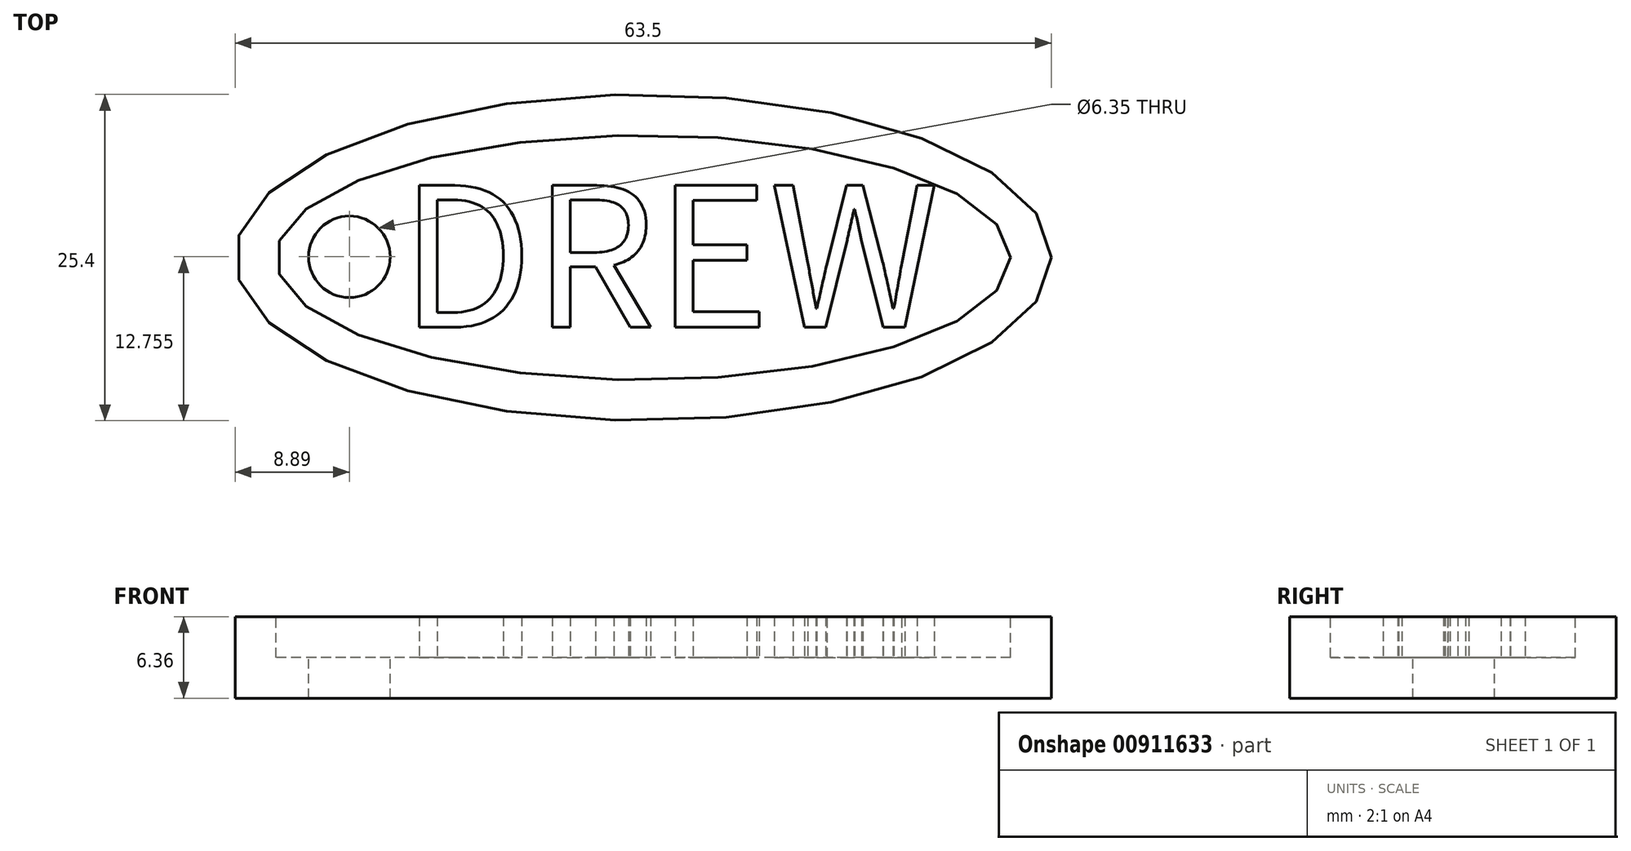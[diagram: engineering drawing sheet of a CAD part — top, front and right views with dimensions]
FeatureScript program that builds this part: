
annotation { "Feature Type Name" : "Feature", "Feature Type Description" : "" }
export const myFeature = defineFeature(function(context is Context, id is Id, definition is map)
    precondition{}
    {
        {
            var Q0;
            Q0=qCreatedBy(makeId("Top.planeOp"),FACE);
            var sketch = newSketch(context, id + "F0", { "sketchPlane" : qUnion([Q0])});
            skEllipse(sketch, "E0", {"center": v(0, 0) * mm, "majorRadius": 31.75 * mm, "minorRadius": 12.7 * mm, "majorAxis": v(1, 0)});
            skSolve(sketch);
        }
        {
            var Q0;
            Q0=makeQuery(id+"F0.imprint","IMPRINT",FACE,{"disambiguationData":[TD([[makeQuery(id+"F0.imprint","IMPRINT",EDGE,{"derivedFrom":sQuery(id+"F0.wireOp",EDGE,"E0")}),1.0]])]});
            extrude(context, id + "F1", {"entities" : qUnion([Q0]), "endBound" : BoundingType.SYMMETRIC, "depth" : 6.35 * mm, "offsetDistance" : 25.4 * mm});
        }
        {
            var Q0;
            Q0=makeQuery(id+"F1.opExtrude","CAP_FACE",FACE,{"disambiguationData":[OSD([sQuery(id+"F0.wireOp",EDGE,"E0")])],"isStart":false});
            var sketch = newSketch(context, id + "F2", { "sketchPlane" : qUnion([Q0])});
            skEllipse(sketch, "E1", {"center": v(0, 0) * mm, "majorRadius": 28.58 * mm, "minorRadius": 9.53 * mm, "majorAxis": v(1, 0)});
            skSolve(sketch);
        }
        {
            var Q0;
            Q0 = qSketchRegion(id + "F2", true);
            extrude(context, id + "F3", {"entities" : qUnion([Q0]), "operationType" : NewBodyOperationType.REMOVE, "oppositeDirection" : true, "depth" : 3.17 * mm, "offsetDistance" : 25.4 * mm});
        }
        {
            var Q0;
            Q0=makeQuery(id+"F3.boolean.opBoolean","COPY",FACE,{"derivedFrom":makeQuery(id+"F3.opExtrude","CAP_FACE",FACE,{"disambiguationData":[OSD([sQuery(id+"F2.wireOp",EDGE,"E1")])],"isStart":false})});
            var sketch = newSketch(context, id + "F4", { "sketchPlane" : qUnion([Q0])});
            skSolve(sketch);
        }
        {
            var Q0;
            Q0=makeQuery(id+"F4.imprint","IMPRINT",FACE,{"disambiguationData":[TD([[makeQuery(id+"F4.imprint","IMPRINT",EDGE,{"derivedFrom":makeQuery(id+"F3.boolean.opBoolean","COPY",EDGE,{"derivedFrom":makeQuery(id+"F3.opExtrude","CAP_EDGE",EDGE,{"disambiguationData":[OSD([sQuery(id+"F2.wireOp",EDGE,"E1")])],"isStart":false})})}),1.0]])]});
            var sketch = newSketch(context, id + "F5", { "sketchPlane" : qUnion([Q0])});
            skText(sketch, "E2", { "text": "DREW", "fontName": "NotoSansCJKsc-Regular.otf"});
            const initialGuessF5  = {"E2": [-0.01893, -0.00542, 1, 0, 0.01084]};
            skSetInitialGuess(sketch, initialGuessF5);
            skSolve(sketch);
        }
        {
            var Q0;
            Q0 = qSketchRegion(id + "F5", true);
            extrude(context, id + "F6", {"entities" : qUnion([Q0]), "operationType" : NewBodyOperationType.ADD, "depth" : 3.17 * mm, "offsetDistance" : 25.4 * mm});
        }
        {
            var Q0;
            Q0=makeQuery(id+"F4.imprint","IMPRINT",FACE,{"disambiguationData":[TD([[makeQuery(id+"F4.imprint","IMPRINT",EDGE,{"derivedFrom":makeQuery(id+"F3.boolean.opBoolean","COPY",EDGE,{"derivedFrom":makeQuery(id+"F3.opExtrude","CAP_EDGE",EDGE,{"disambiguationData":[OSD([sQuery(id+"F2.wireOp",EDGE,"E1")])],"isStart":false})})}),1.0]])]});
            var sketch = newSketch(context, id + "F7", { "sketchPlane" : qUnion([Q0])});
            skCircle(sketch, "E3", {"center": v(-22.86, 0.05) * mm, "radius": 3.18 * mm});
            skSolve(sketch);
        }
        {
            var Q0;
            Q0 = qSketchRegion(id + "F7", true);
            extrude(context, id + "F8", {"entities" : qUnion([Q0]), "operationType" : NewBodyOperationType.REMOVE, "endBound" : BoundingType.THROUGH_ALL, "oppositeDirection" : true, "depth" : 25.4 * mm, "offsetDistance" : 25.4 * mm});
        }
    });
